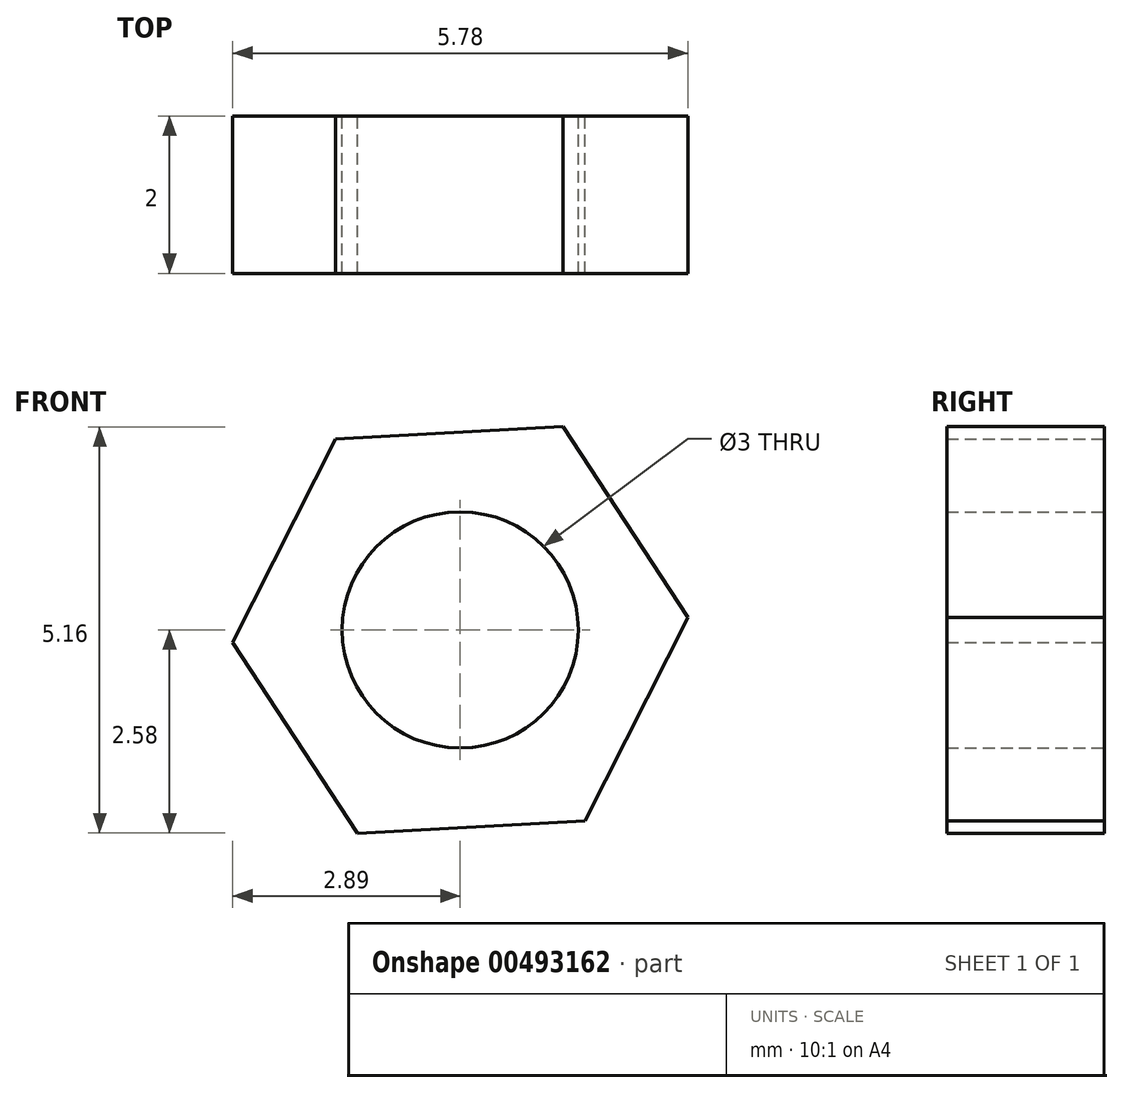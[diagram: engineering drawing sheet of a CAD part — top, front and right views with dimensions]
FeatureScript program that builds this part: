
annotation { "Feature Type Name" : "Feature", "Feature Type Description" : "" }
export const myFeature = defineFeature(function(context is Context, id is Id, definition is map)
    precondition{}
    {
        {
            var Q0;
            Q0=qCreatedBy(makeId("Front.planeOp"),FACE);
            var sketch = newSketch(context, id + "F0", { "sketchPlane" : qUnion([Q0])});
            skCircle(sketch, "E0", {"center": v(0, 0) * mm, "radius": 1.5 * mm});
            skCircle(sketch, "E1.cCircle", {"center": v(0, 0) * mm, "radius": 2.5 * mm, "construction": true});
            skLineSegment(sketch, "E1.0", {"start": v(1.3, 2.58) * mm, "end": v(2.9, 0.16) * mm});
            skLineSegment(sketch, "E1.1", {"start": v(2.9, 0.16) * mm, "end": v(1.58, -2.42) * mm});
            skLineSegment(sketch, "E1.2", {"start": v(1.58, -2.42) * mm, "end": v(-1.3, -2.58) * mm});
            skLineSegment(sketch, "E1.3", {"start": v(-1.3, -2.58) * mm, "end": v(-2.9, -0.16) * mm});
            skLineSegment(sketch, "E1.4", {"start": v(-2.9, -0.16) * mm, "end": v(-1.58, 2.42) * mm});
            skLineSegment(sketch, "E1.5", {"start": v(-1.58, 2.42) * mm, "end": v(1.3, 2.58) * mm});
            skPoint(sketch, "E1.0.midPoint", {"position": v(2.1, 1.37) * mm});
            skSolve(sketch);
        }
        {
            var Q0;
            Q0 = qSketchRegion(id + "F0", true);
            extrude(context, id + "F1", {"entities" : qUnion([Q0]), "depth" : 2 * mm});
        }
    });
